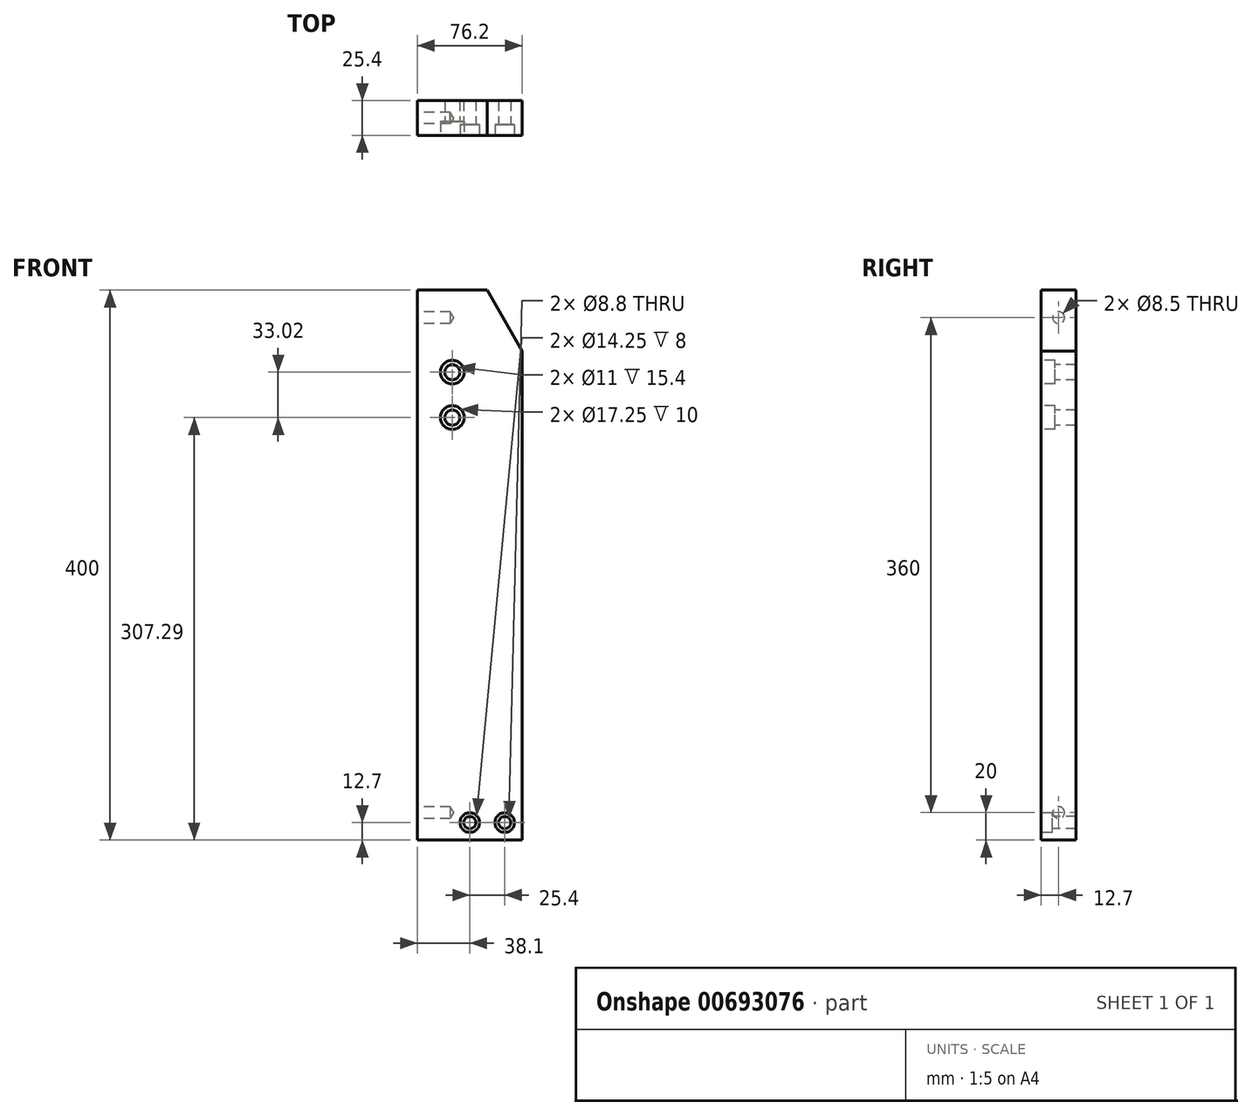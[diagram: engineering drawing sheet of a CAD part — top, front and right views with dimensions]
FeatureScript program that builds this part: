
annotation { "Feature Type Name" : "Feature", "Feature Type Description" : "" }
export const myFeature = defineFeature(function(context is Context, id is Id, definition is map)
    precondition{}
    {
        {
            var Q0;
            Q0=qCreatedBy(makeId("Front.planeOp"),FACE);
            var sketch = newSketch(context, id + "F0", { "sketchPlane" : qUnion([Q0])});
            skLineSegment(sketch, "E0", {"start": v(0, 0) * mm, "end": v(0, 400) * mm});
            skLineSegment(sketch, "E1", {"start": v(0, 400) * mm, "end": v(50.8, 400) * mm});
            skLineSegment(sketch, "E2", {"start": v(0, 0) * mm, "end": v(76.2, 0) * mm});
            skLineSegment(sketch, "E3", {"start": v(76.2, 0) * mm, "end": v(76.2, 355.6) * mm});
            skLineSegment(sketch, "E4", {"start": v(76.2, 355.6) * mm, "end": v(50.8, 400) * mm});
            skSolve(sketch);
        }
        {
            var Q0;
            Q0=makeQuery(id+"F0.imprint","IMPRINT",FACE,{"disambiguationData":[TD([[makeQuery(id+"F0.imprint","IMPRINT",EDGE,{"derivedFrom":sQuery(id+"F0.wireOp",EDGE,"E0")}),-1.0]])]});
            extrude(context, id + "F1", {"entities" : qUnion([Q0]), "depth" : 25.4 * mm, "offsetDistance" : 25.4 * mm});
        }
        {
            var Q0;
            Q0=makeQuery(id+"F1.opExtrude","SWEPT_FACE",FACE,{"disambiguationData":[OSD([sQuery(id+"F0.wireOp",EDGE,"E0")])]});
            var sketch = newSketch(context, id + "F2", { "sketchPlane" : qUnion([Q0])});
            skLineSegment(sketch, "E5", {"start": v(12.7, 0) * mm, "end": v(12.7, 20) * mm});
            skLineSegment(sketch, "E6", {"start": v(12.7, 400) * mm, "end": v(12.7, 380) * mm});
            skSolve(sketch);
        }
        {
            var Q0;
            Q0=sQuery(id+"F2.wireOp",VERTEX,"E5.end");
            var Q1;
            Q1=sQuery(id+"F2.wireOp",VERTEX,"E6.end");
            var Q2;
            Q2=makeQuery(id+"F1.opExtrude","SWEPT_BODY",BODY,{"disambiguationData":[OSD([sQuery(id+"F0.wireOp",EDGE,"E0"),sQuery(id+"F0.wireOp",EDGE,"E1"),sQuery(id+"F0.wireOp",EDGE,"E2"),sQuery(id+"F0.wireOp",EDGE,"E3"),sQuery(id+"F0.wireOp",EDGE,"E4")])]});
            hole(context, id + "F3", {"style" : HoleStyle.SIMPLE, "endStyle" : HoleEndStyle.BLIND, "standardTappedOrClearance" : lookupTablePath({ "standard" : "ISO", "engagement" : "75%", "pitch" : "1.5 mm", "size" : "M10", "type" : "Tapped" }), "standardBlindInLast" : lookupTablePath({ "standard" : "ISO", "engagement" : "75%", "pitch" : "1.5 mm", "size" : "M10", "type" : "Tapped" }), "holeDiameter" : 8.5 * mm, "majorDiameter" : 10 * mm, "showTappedDepth" : true, "holeDepth" : 23.9 * mm, "tappedDepth" : 19.4 * mm, "tapClearance" : 3, "locations" : qUnion([Q0, Q1]), "scope" : qUnion([Q2])});
        }
        {
            var Q0;
            Q0=makeQuery(id+"F1.opExtrude","CAP_FACE",FACE,{"disambiguationData":[OSD([sQuery(id+"F0.wireOp",EDGE,"E0"),sQuery(id+"F0.wireOp",EDGE,"E1"),sQuery(id+"F0.wireOp",EDGE,"E2"),sQuery(id+"F0.wireOp",EDGE,"E3"),sQuery(id+"F0.wireOp",EDGE,"E4")])],"isStart":false});
            var sketch = newSketch(context, id + "F4", { "sketchPlane" : qUnion([Q0])});
            skLineSegment(sketch, "E7", {"start": v(76.2, 0) * mm, "end": v(76.2, 12.7) * mm});
            skLineSegment(sketch, "E8", {"start": v(63.5, 12.7) * mm, "end": v(76.2, 12.7) * mm});
            skLineSegment(sketch, "E9", {"start": v(38.1, 12.7) * mm, "end": v(63.5, 12.7) * mm});
            skSolve(sketch);
        }
        {
            var Q0;
            Q0=sQuery(id+"F4.wireOp",VERTEX,"E9.start");
            var Q1;
            Q1=sQuery(id+"F4.wireOp",VERTEX,"E9.end");
            var Q2;
            Q2=makeQuery(id+"F1.opExtrude","SWEPT_BODY",BODY,{"disambiguationData":[OSD([sQuery(id+"F0.wireOp",EDGE,"E0"),sQuery(id+"F0.wireOp",EDGE,"E1"),sQuery(id+"F0.wireOp",EDGE,"E2"),sQuery(id+"F0.wireOp",EDGE,"E3"),sQuery(id+"F0.wireOp",EDGE,"E4")])]});
            hole(context, id + "F5", {"style" : HoleStyle.C_BORE, "endStyle" : HoleEndStyle.THROUGH, "standardTappedOrClearance" : lookupTablePath({ "standard" : "ISO", "fit" : "Normal", "size" : "M8", "type" : "Clearance" }), "standardBlindInLast" : lookupTablePath({ "fit" : "Standard", "standard" : "ISO", "size" : "M8", "type" : "Clearance" }), "holeDiameter" : 8.8 * mm, "cBoreDiameter" : 14.25 * mm, "cBoreDepth" : 8 * mm, "majorDiameter" : 8 * mm, "tappedDepth" : 19.4 * mm, "tapClearance" : 3, "locations" : qUnion([Q0, Q1]), "scope" : qUnion([Q2])});
        }
        {
            var Q0;
            Q0=makeQuery(id+"F1.opExtrude","CAP_FACE",FACE,{"disambiguationData":[OSD([sQuery(id+"F0.wireOp",EDGE,"E0"),sQuery(id+"F0.wireOp",EDGE,"E1"),sQuery(id+"F0.wireOp",EDGE,"E2"),sQuery(id+"F0.wireOp",EDGE,"E3"),sQuery(id+"F0.wireOp",EDGE,"E4")])],"isStart":false});
            var sketch = newSketch(context, id + "F6", { "sketchPlane" : qUnion([Q0])});
            skLineSegment(sketch, "E10", {"start": v(25.4, 400) * mm, "end": v(25.4, 340.3) * mm});
            skLineSegment(sketch, "E11", {"start": v(25.4, 340.3) * mm, "end": v(25.4, 307.3) * mm});
            skSolve(sketch);
        }
        {
            var Q0;
            Q0=sQuery(id+"F6.wireOp",VERTEX,"E11.start");
            var Q1;
            Q1=sQuery(id+"F6.wireOp",VERTEX,"E11.end");
            var Q2;
            Q2=makeQuery(id+"F1.opExtrude","SWEPT_BODY",BODY,{"disambiguationData":[OSD([sQuery(id+"F0.wireOp",EDGE,"E0"),sQuery(id+"F0.wireOp",EDGE,"E1"),sQuery(id+"F0.wireOp",EDGE,"E2"),sQuery(id+"F0.wireOp",EDGE,"E3"),sQuery(id+"F0.wireOp",EDGE,"E4")])]});
            hole(context, id + "F7", {"style" : HoleStyle.C_BORE, "endStyle" : HoleEndStyle.THROUGH, "standardTappedOrClearance" : lookupTablePath({ "standard" : "ISO", "fit" : "Normal", "size" : "M10", "type" : "Clearance" }), "standardBlindInLast" : lookupTablePath({ "fit" : "Standard", "standard" : "ISO", "size" : "M10", "type" : "Clearance" }), "holeDiameter" : 11 * mm, "cBoreDiameter" : 17.25 * mm, "cBoreDepth" : 10 * mm, "majorDiameter" : 10 * mm, "tappedDepth" : 19.38 * mm, "tapClearance" : 3, "locations" : qUnion([Q0, Q1]), "scope" : qUnion([Q2])});
        }
    });
